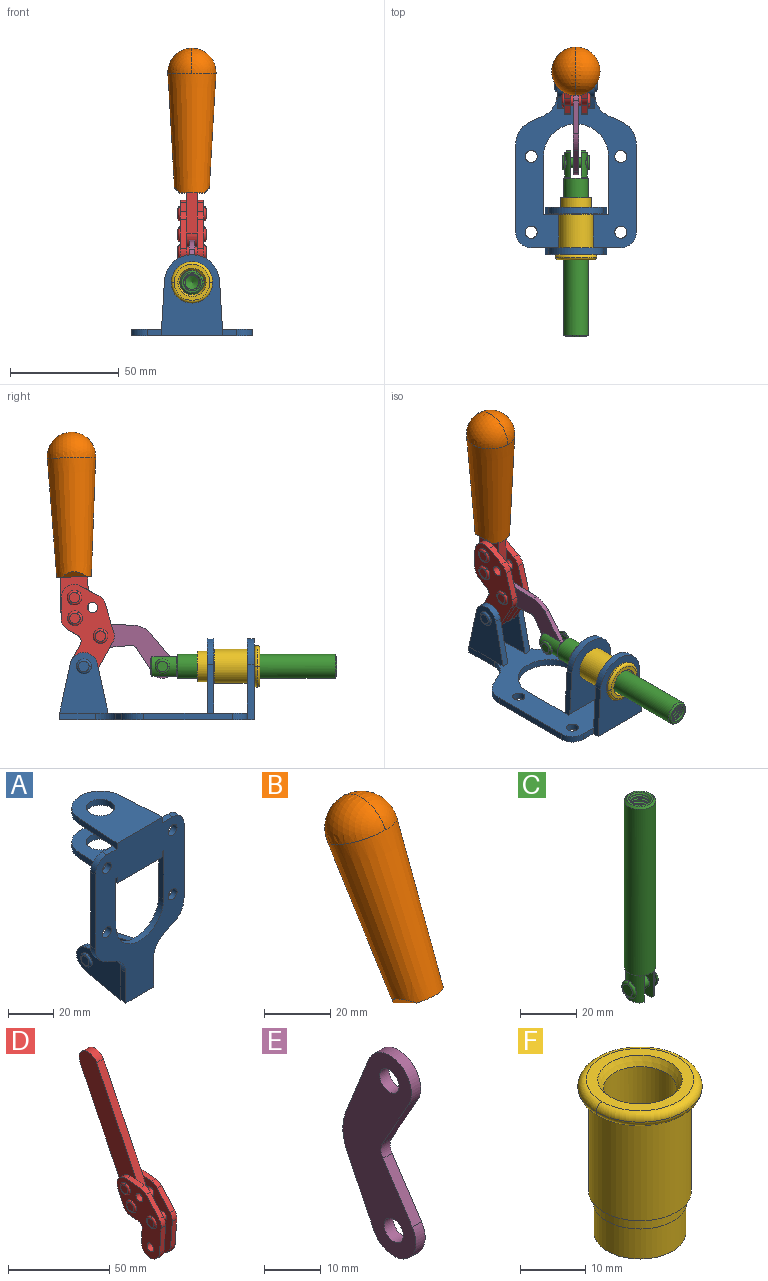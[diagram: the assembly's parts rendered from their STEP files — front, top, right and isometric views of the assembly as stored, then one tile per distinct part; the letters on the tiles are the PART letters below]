
ASSEMBLY  parts=6 mates=6
PART A: 55 faces, bbox 55.7x37.4x89.8 mm
  f0: torus R=2.41mm, axis (-1,0,0), area 15mm2, adj f11,f15,f25
  f1: torus R=2.41mm, axis (-1,0,0), area 15mm2, adj f10,f12,f22
  f2: cylinder r=2.78mm len=5.56mm, axis (0,-1,0), area 54.2mm2, adj f30,f54
  f3: cylinder r=14.99mm len=29.97mm, axis (0,-1,0), area 145.9mm2, adj f30,f49,f53,f54
  f4: cylinder r=2.78mm len=5.56mm, axis (0,-1,0), area 54.2mm2, adj f30,f54
  f5: cylinder r=2.78mm len=5.56mm, axis (0,-1,0), area 54.2mm2, adj f30,f54
  f6: cylinder r=2.78mm len=5.56mm, axis (0,-1,0), area 54.2mm2, adj f30,f54
  f7: cylinder r=6.35mm len=12.7mm, axis (0,0,1), area 123.6mm2, adj f27,f51
  f8: cylinder r=6.35mm len=12.7mm, axis (0,0,-1), area 124.7mm2, adj f21,f35
  f9: cylinder r=2.41mm len=11.18mm, axis (-1,0,0), area 169.4mm2, adj f16,f19
  f10: plane 4.83x4.83mm, normal (1,0,0), area 18.3mm2, adj f1,f12
  f11: plane 4.83x4.83mm, normal (-1,0,0), area 18.3mm2, adj f0,f15
  f12: torus R=2.41mm, axis (-1,0,0), area 15mm2, adj f1,f10,f22
  f13: cylinder r=6.35mm len=12.41mm, axis (1,0,0), area 53.4mm2, adj f18,f19,f22,f23
  f14: cylinder r=6.35mm len=12.41mm, axis (-1,0,0), area 53.4mm2, adj f16,f17,f24,f25
  f15: torus R=2.41mm, axis (-1,0,0), area 15mm2, adj f0,f11,f25
  f16: plane 27.86x22.35mm, normal (1,0,0), area 425.4mm2, adj f9,f14,f17,f24,f30
  f17: plane 22.86x4.97mm, normal (0,0.21,0.98), area 72.5mm2, adj f14,f16,f25,f30
  f18: plane 22.86x4.97mm, normal (0,0.21,0.98), area 72.5mm2, adj f13,f19,f22,f30
  f19: plane 27.86x22.35mm, normal (-1,0,0), area 425.4mm2, adj f9,f13,f18,f23,f30
  f20: cylinder r=12.7mm len=25.35mm, axis (0,0,-1), area 119.8mm2, adj f21,f34,f35,f36
  f21: plane 34.21x28.07mm, normal (0,0,-1), area 702.4mm2, adj f8,f20,f30,f34,f36
  f22: plane 27.96x22.45mm, normal (1,0,0), area 407.2mm2, adj f1,f12,f13,f18,f23,f30,f42,f43
  f23: plane 22.86x4.97mm, normal (0,0.21,-0.98), area 72.5mm2, adj f13,f19,f22,f44
  f24: plane 22.86x4.97mm, normal (0,0.21,-0.98), area 72.5mm2, adj f14,f16,f25,f44
  f25: plane 27.86x22.35mm, normal (-1,0,0), area 407.1mm2, adj f0,f14,f15,f17,f24,f30,f45,f46
  f26: plane 3.1x0.95mm, normal (0,0,-1), area 2.7mm2, adj f30,f49,f50,f54
  f27: plane 34.21x28.07mm, normal (0,0,1), area 702.4mm2, adj f7,f28,f30,f50,f52
  f28: cylinder r=12.7mm len=25.35mm, axis (0,0,1), area 118.8mm2, adj f27,f50,f51,f52
  f29: plane 3.1x0.95mm, normal (0,0,-1), area 2.7mm2, adj f30,f52,f53,f54
  f30: plane 86.54x55.63mm, normal (0,1,0), area 2362.9mm2, adj f2,f3,f4,f5,f6,f16,f17,f18
  f31: plane 40.56x3.1mm, normal (-1,0,0), area 125.7mm2, adj f30,f32,f48,f54
  f32: cylinder r=7.11mm len=7.11mm, axis (0,-1,0), area 34.6mm2, adj f30,f31,f33,f54
  f33: plane 6.67x3.1mm, normal (0,0,1), area 20.4mm2, adj f30,f32,f34,f54
  f34: plane 25.39x3.13mm, normal (-1,0.06,0), area 79.5mm2, adj f20,f21,f33,f35,f54
  f35: plane 37.31x28.45mm, normal (0,0,1), area 789.9mm2, adj f8,f20,f34,f36,f54
  f36: plane 25.39x3.13mm, normal (1,0.06,0), area 79.5mm2, adj f20,f21,f35,f37,f54
  f37: plane 6.67x3.1mm, normal (0,0,1), area 20.4mm2, adj f30,f36,f38,f54
  f38: cylinder r=7.11mm len=7.11mm, axis (0,-1,0), area 34.6mm2, adj f30,f37,f39,f54
  f39: plane 40.56x3.1mm, normal (1,0,0), area 125.7mm2, adj f30,f38,f40,f54
  f40: cylinder r=11.18mm len=10.16mm, axis (0,-1,0), area 39.5mm2, adj f30,f39,f41,f54
  f41: plane 6.09x3.1mm, normal (0.42,0,-0.91), area 20.8mm2, adj f30,f40,f42,f54
  f42: cylinder r=11.18mm len=9.41mm, axis (0,-1,0), area 37.2mm2, adj f22,f30,f41,f43,f54
  f43: plane 16.5x3.1mm, normal (1,0,0), area 51.1mm2, adj f22,f42,f44,f54
  f44: plane 17.37x3.1mm, normal (0,0,-1), area 53.8mm2, adj f23,f24,f30,f43,f45,f54
  f45: plane 16.5x3.1mm, normal (-1,0,0), area 51.1mm2, adj f25,f44,f46,f54
  f46: cylinder r=11.18mm len=9.41mm, axis (0,-1,0), area 37.2mm2, adj f25,f30,f45,f47,f54
  f47: plane 6.09x3.1mm, normal (-0.42,0,-0.91), area 20.8mm2, adj f30,f46,f48,f54
  f48: cylinder r=11.18mm len=10.16mm, axis (0,-1,0), area 39.5mm2, adj f30,f31,f47,f54
  f49: plane 26.54x3.1mm, normal (-1,0,0), area 82.3mm2, adj f3,f26,f30,f54
  f50: plane 25.39x3.1mm, normal (1,0.06,0), area 78.8mm2, adj f26,f27,f28,f51,f54
  f51: plane 37.31x28.45mm, normal (0,0,-1), area 789.9mm2, adj f7,f28,f50,f52,f54
  f52: plane 25.39x3.1mm, normal (-1,0.06,0), area 78.8mm2, adj f27,f28,f29,f51,f54
  f53: plane 26.54x3.1mm, normal (1,0,0), area 82.3mm2, adj f3,f29,f30,f54
  f54: plane 89.66x55.63mm, normal (0,-1,0), area 2678.5mm2, adj f2,f3,f4,f5,f6,f26,f29,f31
PART B: 11 faces, bbox 22.3x42.6x64.5 mm
  f0: sphere r=11.13mm, area 411.4mm2, adj f1,f8
  f1: cone r=11.11mm half-angle=3.3deg, axis (0,0.44,0.9), area 3251.8mm2, adj f0,f7,f8,f9,f10
  f2: cylinder r=6.16mm len=11.7mm, axis (1,0,0), area 89.5mm2, adj f3,f4,f5,f6
  f3: plane 60.23x36.75mm, normal (-1,0,0), area 763.6mm2, adj f2,f4,f6,f10
  f4: plane 51.37x25.05mm, normal (0,0.9,-0.44), area 264.2mm2, adj f2,f3,f5,f10
  f5: plane 60.23x36.75mm, normal (1,0,0), area 763.6mm2, adj f2,f4,f6,f10
  f6: plane 51.37x25.05mm, normal (0,-0.9,0.44), area 264.2mm2, adj f2,f3,f5,f10
  f7: plane 9.95x5.95mm, normal (0.71,-0.31,-0.64), area 25.8mm2, adj f1,f10
  f8: sphere r=11.13mm, area 411.4mm2, adj f0,f1
  f9: plane 9.95x5.95mm, normal (-0.71,-0.31,-0.64), area 25.8mm2, adj f1,f10
  f10: plane 14.27x11.38mm, normal (0,-0.44,-0.9), area 106.7mm2, adj f1,f3,f4,f5,f6,f7,f9
PART C: 48 faces, bbox 12.6x11.1x86.1 mm
  f0: torus R=2.41mm, axis (-1,0,0), area 15mm2, adj f30,f32,f34
  f1: torus R=2.41mm, axis (-1,0,0), area 15mm2, adj f29,f31,f33
  f2: cylinder r=5.54mm len=72.39mm, axis (0,0,1), area 2518.5mm2, adj f3,f4,f42,f43
  f3: cone r=5.54mm half-angle=45deg, axis (0,0,1), area 7.6mm2, adj f2,f5,f41
  f4: cone r=5.54mm half-angle=45deg, axis (0,0,-1), area 34.9mm2, adj f2,f39
  f5: cylinder r=5.08mm len=11.48mm, axis (0,0,1), area 108.3mm2, adj f3,f7,f8,f41
  f6: cylinder r=2.41mm len=4.83mm, axis (-1,0,0), area 71.2mm2, adj f40,f41
  f7: cylinder r=2.41mm len=4.83mm, axis (-1,0,0), area 7.6mm2, adj f5,f34
  f8: cone r=5.08mm half-angle=45deg, axis (0,0,1), area 10.6mm2, adj f5,f37,f41
  f9: cone r=3.98mm half-angle=45deg, axis (0,0,1), area 17.6mm2, adj f27,f39,f45,f46,f47
  f10: cylinder r=2.41mm len=4.83mm, axis (-1,0,0), area 7.6mm2, adj f33,f38
  f11: cylinder r=3.2mm len=6.4mm, axis (0,0,1), area 78.4mm2, adj f12,f28,f44,f45,f47
  f12: cylinder r=3.2mm len=6.4mm, axis (0,0,1), area 10.5mm2, adj f11,f13,f45,f47
  f13: cylinder r=3.2mm len=6.4mm, axis (0,0,1), area 10.5mm2, adj f12,f14,f45,f47
  f14: cylinder r=3.2mm len=6.4mm, axis (0,0,1), area 10.5mm2, adj f13,f15,f45,f47
  f15: cylinder r=3.2mm len=6.4mm, axis (0,0,1), area 10.5mm2, adj f14,f16,f45,f47
  f16: cylinder r=3.2mm len=6.4mm, axis (0,0,1), area 10.5mm2, adj f15,f17,f45,f47
  f17: cylinder r=3.2mm len=6.4mm, axis (0,0,1), area 10.5mm2, adj f16,f18,f45,f47
  f18: cylinder r=3.2mm len=6.4mm, axis (0,0,1), area 10.5mm2, adj f17,f19,f45,f47
  f19: cylinder r=3.2mm len=6.4mm, axis (0,0,1), area 10.5mm2, adj f18,f20,f45,f47
  f20: cylinder r=3.2mm len=6.4mm, axis (0,0,1), area 10.5mm2, adj f19,f21,f45,f47
  f21: cylinder r=3.2mm len=6.4mm, axis (0,0,1), area 10.5mm2, adj f20,f22,f45,f47
  f22: cylinder r=3.2mm len=6.4mm, axis (0,0,1), area 10.5mm2, adj f21,f23,f45,f47
  f23: cylinder r=3.2mm len=6.4mm, axis (0,0,1), area 10.5mm2, adj f22,f24,f45,f47
  f24: cylinder r=3.2mm len=6.4mm, axis (0,0,1), area 10.5mm2, adj f23,f25,f45,f47
  f25: cylinder r=3.2mm len=6.4mm, axis (0,0,1), area 10.5mm2, adj f24,f26,f45,f47
  f26: cylinder r=3.2mm len=6.4mm, axis (0,0,1), area 10.5mm2, adj f25,f27,f45,f47
  f27: cylinder r=3.2mm len=6.4mm, axis (0,0,1), area 7.4mm2, adj f9,f26,f45,f47
  f28: cone r=3.2mm half-angle=60deg, axis (0,0,1), area 37.2mm2, adj f11
  f29: plane 4.83x4.83mm, normal (-1,0,0), area 18.3mm2, adj f1,f31
  f30: plane 4.83x4.83mm, normal (1,0,0), area 18.3mm2, adj f0,f32
  f31: torus R=2.41mm, axis (-1,0,0), area 15mm2, adj f1,f29,f33
  f32: torus R=2.41mm, axis (-1,0,0), area 15mm2, adj f0,f30,f34
  f33: plane 6.83x6.83mm, normal (1,0,0), area 18.3mm2, adj f1,f10,f31
  f34: plane 6.83x6.83mm, normal (-1,0,0), area 18.3mm2, adj f0,f7,f32
  f35: cone r=5.08mm half-angle=45deg, axis (0,0,1), area 10.6mm2, adj f36,f38,f40
  f36: plane 7.25x1.97mm, normal (0,0,-1), area 10mm2, adj f35,f40
  f37: plane 7.25x1.97mm, normal (0,0,-1), area 10mm2, adj f8,f41
  f38: cylinder r=5.08mm len=11.48mm, axis (0,0,1), area 108.3mm2, adj f10,f35,f40,f42
  f39: plane 9.55x9.55mm, normal (0,0,1), area 22mm2, adj f4,f9
  f40: plane 12.76x10.09mm, normal (1,0,0), area 95.7mm2, adj f6,f35,f36,f38,f42,f43
  f41: plane 12.76x10.09mm, normal (-1,0,0), area 95.7mm2, adj f3,f5,f6,f8,f37,f43
  f42: cone r=5.54mm half-angle=45deg, axis (0,0,1), area 7.6mm2, adj f2,f38,f40
  f43: plane 11.07x4.7mm, normal (0,0,-1), area 50.4mm2, adj f2,f40,f41
  f44: plane 0.89x0.62mm, normal (-1,0,0), area 0.3mm2, adj f11,f45,f46,f47
  f45: bspline ~24.8x7.63mm, area 266.6mm2, adj f9,f11,f12,f13,f14,f15,f16,f17
  f46: bspline ~24.87x7.63mm, area 73.6mm2, adj f9,f44,f45,f47
  f47: bspline ~24.98x7.63mm, area 272.5mm2, adj f9,f11,f12,f13,f14,f15,f16,f17
PART D: 59 faces, bbox 12.9x60.2x99.6 mm
  f0: torus R=2.39mm, axis (-1,0,0), area 14.9mm2, adj f20,f43,f51
  f1: torus R=2.39mm, axis (-1,0,0), area 14.9mm2, adj f19,f42,f51
  f2: torus R=2.39mm, axis (-1,0,0), area 14.9mm2, adj f18,f35,f51
  f3: torus R=2.39mm, axis (-1,0,0), area 14.9mm2, adj f14,f17,f23
  f4: torus R=2.39mm, axis (-1,0,0), area 14.9mm2, adj f13,f16,f23
  f5: torus R=2.39mm, axis (-1,0,0), area 14.9mm2, adj f12,f15,f23
  f6: cylinder r=2.39mm len=4.78mm, axis (1,0,0), area 46.5mm2, adj f48,f50,f51
  f7: cylinder r=2.39mm len=4.78mm, axis (1,0,0), area 46.5mm2, adj f50,f51
  f8: cylinder r=6.35mm len=12.68mm, axis (1,0,0), area 61.8mm2, adj f38,f39,f50,f51
  f9: cylinder r=2.39mm len=4.78mm, axis (-1,0,0), area 70.5mm2, adj f46,f50
  f10: cylinder r=2.39mm len=4.78mm, axis (-1,0,0), area 46.5mm2, adj f23,f45,f46
  f11: cylinder r=2.39mm len=4.78mm, axis (-1,0,0), area 46.5mm2, adj f23,f46
  f12: plane 4.78x4.78mm, normal (1,0,0), area 17.9mm2, adj f5,f15
  f13: plane 4.78x4.78mm, normal (1,0,0), area 17.9mm2, adj f4,f16
  f14: plane 4.78x4.78mm, normal (1,0,0), area 17.9mm2, adj f3,f17
  f15: torus R=2.39mm, axis (-1,0,0), area 14.9mm2, adj f5,f12,f23
  f16: torus R=2.39mm, axis (-1,0,0), area 14.9mm2, adj f4,f13,f23
  f17: torus R=2.39mm, axis (-1,0,0), area 14.9mm2, adj f3,f14,f23
  f18: plane 4.78x4.78mm, normal (-1,0,0), area 17.9mm2, adj f2,f35
  f19: plane 4.78x4.78mm, normal (-1,0,0), area 17.9mm2, adj f1,f42
  f20: plane 4.78x4.78mm, normal (-1,0,0), area 17.9mm2, adj f0,f43
  f21: plane 2.26x0.2mm, normal (1,0,0), area 0.2mm2, adj f31,f44
  f22: plane 2.26x0.2mm, normal (-1,0,0), area 0.2mm2, adj f41,f44
  f23: plane 39.37x30.77mm, normal (1,0,0), area 565.5mm2, adj f3,f4,f5,f10,f11,f15,f16,f17
  f24: cylinder r=6.1mm len=4.15mm, axis (-1,0,0), area 14.7mm2, adj f23,f25,f32,f46
  f25: plane 10.25x9.01mm, normal (0,-0.75,0.66), area 42.3mm2, adj f23,f24,f26,f46
  f26: cylinder r=6.35mm len=4.64mm, axis (-1,0,0), area 15.6mm2, adj f23,f25,f27,f46
  f27: plane 15.84x3.1mm, normal (0,-1,-0.07), area 49.2mm2, adj f23,f26,f28,f46
  f28: cylinder r=6.35mm len=12.68mm, axis (-1,0,0), area 61.8mm2, adj f23,f27,f29,f46
  f29: plane 8.11x3.1mm, normal (0,1,0.07), area 25.2mm2, adj f23,f28,f30,f46
  f30: cylinder r=3.05mm len=3.25mm, axis (-1,0,0), area 14.8mm2, adj f23,f29,f31,f46
  f31: plane 5.99x3.1mm, normal (0,0.07,-1), area 18.6mm2, adj f21,f23,f30,f44,f46
  f32: plane 9.5x3.1mm, normal (0,-0.07,1), area 29.5mm2, adj f23,f24,f33,f46,f47
  f33: cylinder r=6.1mm len=8.63mm, axis (-1,0,0), area 39.1mm2, adj f23,f32,f34,f47
  f34: plane 8.65x3.96mm, normal (0,0.91,-0.42), area 29.5mm2, adj f23,f33,f44,f47
  f35: torus R=2.39mm, axis (-1,0,0), area 14.9mm2, adj f2,f18,f51
  f36: plane 10.25x9.01mm, normal (0,-0.75,0.66), area 42.3mm2, adj f37,f49,f50,f51
  f37: cylinder r=6.35mm len=4.64mm, axis (1,0,0), area 15.6mm2, adj f36,f38,f50,f51
  f38: plane 15.84x3.1mm, normal (0,-1,-0.07), area 49.2mm2, adj f8,f37,f50,f51
  f39: plane 8.11x3.1mm, normal (0,1,0.07), area 25.2mm2, adj f8,f40,f50,f51
  f40: cylinder r=3.05mm len=3.25mm, axis (1,0,0), area 14.8mm2, adj f39,f41,f50,f51
  f41: plane 5.99x3.1mm, normal (0,0.07,-1), area 18.6mm2, adj f22,f40,f44,f50,f51
  f42: torus R=2.39mm, axis (-1,0,0), area 14.9mm2, adj f1,f19,f51
  f43: torus R=2.39mm, axis (-1,0,0), area 14.9mm2, adj f0,f20,f51
  f44: cylinder r=6.35mm len=12.12mm, axis (-1,0,0), area 128.9mm2, adj f21,f22,f23,f31,f34,f41,f46,f47
  f45: plane 2.65x1.35mm, normal (1,0,0), area 1mm2, adj f10,f55
  f46: plane 39.08x20.42mm, normal (-1,0,0), area 412.5mm2, adj f9,f10,f11,f24,f25,f26,f27,f28
  f47: plane 77.62x39.82mm, normal (1,0,0), area 850mm2, adj f32,f33,f34,f44,f53,f54,f55
  f48: plane 2.65x1.35mm, normal (-1,0,0), area 1mm2, adj f6,f55
  f49: cylinder r=6.1mm len=4.15mm, axis (1,0,0), area 14.7mm2, adj f36,f50,f51,f56
  f50: plane 39.08x20.42mm, normal (1,0,0), area 412.5mm2, adj f6,f7,f8,f9,f36,f37,f38,f39
  f51: plane 39.37x30.77mm, normal (-1,0,0), area 565.5mm2, adj f0,f1,f2,f6,f7,f8,f35,f36
  f52: plane 8.65x3.96mm, normal (0,0.91,-0.42), area 29.5mm2, adj f44,f51,f57,f58
  f53: plane 68.49x33.4mm, normal (0,0.9,-0.44), area 358.1mm2, adj f44,f47,f54,f58
  f54: cylinder r=6.35mm len=12.06mm, axis (1,0,0), area 93.7mm2, adj f47,f53,f55,f58
  f55: plane 68.49x33.4mm, normal (0,-0.9,0.44), area 358.1mm2, adj f44,f45,f46,f47,f48,f50,f54,f58
  f56: plane 9.5x3.1mm, normal (0,-0.07,1), area 29.5mm2, adj f49,f50,f51,f57,f58
  f57: cylinder r=6.1mm len=8.63mm, axis (1,0,0), area 39.1mm2, adj f51,f52,f56,f58
  f58: plane 77.62x39.82mm, normal (-1,0,0), area 850mm2, adj f44,f52,f53,f54,f55,f56,f57
PART E: 12 faces, bbox 2.3x18.2x42.8 mm
  f0: cylinder r=2.4mm len=4.8mm, axis (1,0,0), area 34.9mm2, adj f4,f11
  f1: cylinder r=10.41mm len=8.47mm, axis (1,0,0), area 20.2mm2, adj f4,f9,f10,f11
  f2: cylinder r=3.05mm len=3.16mm, axis (1,0,0), area 7.7mm2, adj f4,f6,f7,f11
  f3: cylinder r=2.4mm len=4.8mm, axis (1,0,0), area 34.9mm2, adj f4,f11
  f4: plane 42.81x18.23mm, normal (-1,0,0), area 414.1mm2, adj f0,f1,f2,f3,f5,f6,f7,f8
  f5: cylinder r=5.54mm len=10.67mm, axis (1,0,0), area 41.8mm2, adj f4,f6,f10,f11
  f6: plane 11.66x6.53mm, normal (0,-0.87,-0.49), area 30.9mm2, adj f2,f4,f5,f11
  f7: plane 11.17x7.33mm, normal (0,-0.84,0.55), area 30.9mm2, adj f2,f4,f8,f11
  f8: cylinder r=5.54mm len=10.51mm, axis (1,0,0), area 41.8mm2, adj f4,f7,f9,f11
  f9: plane 13.67x6.67mm, normal (0,0.9,-0.44), area 35.1mm2, adj f1,f4,f8,f11
  f10: plane 14.1x5.7mm, normal (0,0.93,0.37), area 35.1mm2, adj f1,f4,f5,f11
  f11: plane 42.81x18.23mm, normal (1,0,0), area 414.1mm2, adj f0,f1,f2,f3,f5,f6,f7,f8
PART F: 15 faces, bbox 20.6x20.6x28.7 mm
  f0: torus R=8.26mm, axis (0,0,1), area 56.8mm2, adj f1,f10,f12
  f1: torus R=8.26mm, axis (0,0,1), area 56.8mm2, adj f0,f6,f13
  f2: cylinder r=5.59mm len=25.91mm, axis (0,0,1), area 909.6mm2, adj f3,f4
  f3: cone r=6.86mm half-angle=45deg, axis (0,0,-1), area 70.2mm2, adj f2,f14
  f4: cone r=6.47mm half-angle=30deg, axis (0,0,1), area 66.7mm2, adj f2,f13
  f5: cylinder r=7.04mm len=14.07mm, axis (0,0,1), area 252.6mm2, adj f11,f14
  f6: torus R=8.26mm, axis (0,0,1), area 56.8mm2, adj f1,f12,f13
  f7: cylinder r=7.16mm len=14.33mm, axis (0,0,1), area 91.5mm2, adj f9,f11
  f8: cylinder r=7.86mm len=18.42mm, axis (0,0,1), area 909.6mm2, adj f9,f10
  f9: plane 15.72x15.72mm, normal (0,0,-1), area 33mm2, adj f7,f8
  f10: plane 16.51x16.51mm, normal (0,0,-1), area 19.9mm2, adj f0,f8,f12
  f11: plane 14.33x14.33mm, normal (0,0,-1), area 5.7mm2, adj f5,f7
  f12: torus R=8.26mm, axis (0,0,1), area 56.8mm2, adj f0,f6,f10
  f13: plane 16.51x16.51mm, normal (0,0,1), area 82.7mm2, adj f1,f4,f6
  f14: plane 14.07x14.07mm, normal (0,0,-1), area 7.8mm2, adj f3,f5
PLACE A rot(axis=(1,0,0),90deg) t=(4.59,3.07,-0.87)mm fixed
PLACE B rot(axis=(1,0,0),24.8deg) t=(4.55,-0.63,42.57)mm
PLACE C rot(axis=(1,0,0),90deg) t=(4.59,14.46,-0.87)mm
PLACE D rot(axis=(1,0,0),24.8deg) t=(4.59,-0.63,42.57)mm
PLACE E rot(axis=(0,-0.54,-0.84),180deg) t=(4.59,23.39,8.88)mm
PLACE F rot(axis=(1,0,0),90deg) t=(4.59,3.07,-0.87)mm
MATE revolute D.f7 <-> A.f0  axis (1,0,0) through (4.59,35.17,23.74)mm
MATE fastened A.f7 <-> F.f2  axis (0,-1,0) through (4.59,-43.32,23.74)mm
MATE slider C.f2 <-> F.f2  axis (0,-1,0) through (4.59,-44.32,23.74)mm
MATE revolute E.f5 <-> D.f4  axis (-1,0,0) through (4.59,27.52,37.66)mm
MATE fastened B.f2 <-> D.f54  axis (1,0,0) through (2.24,40.91,122.07)mm
MATE revolute E.f3 <-> C.f6  axis (-1,0,0) through (4.59,-1.02,23.74)mm
